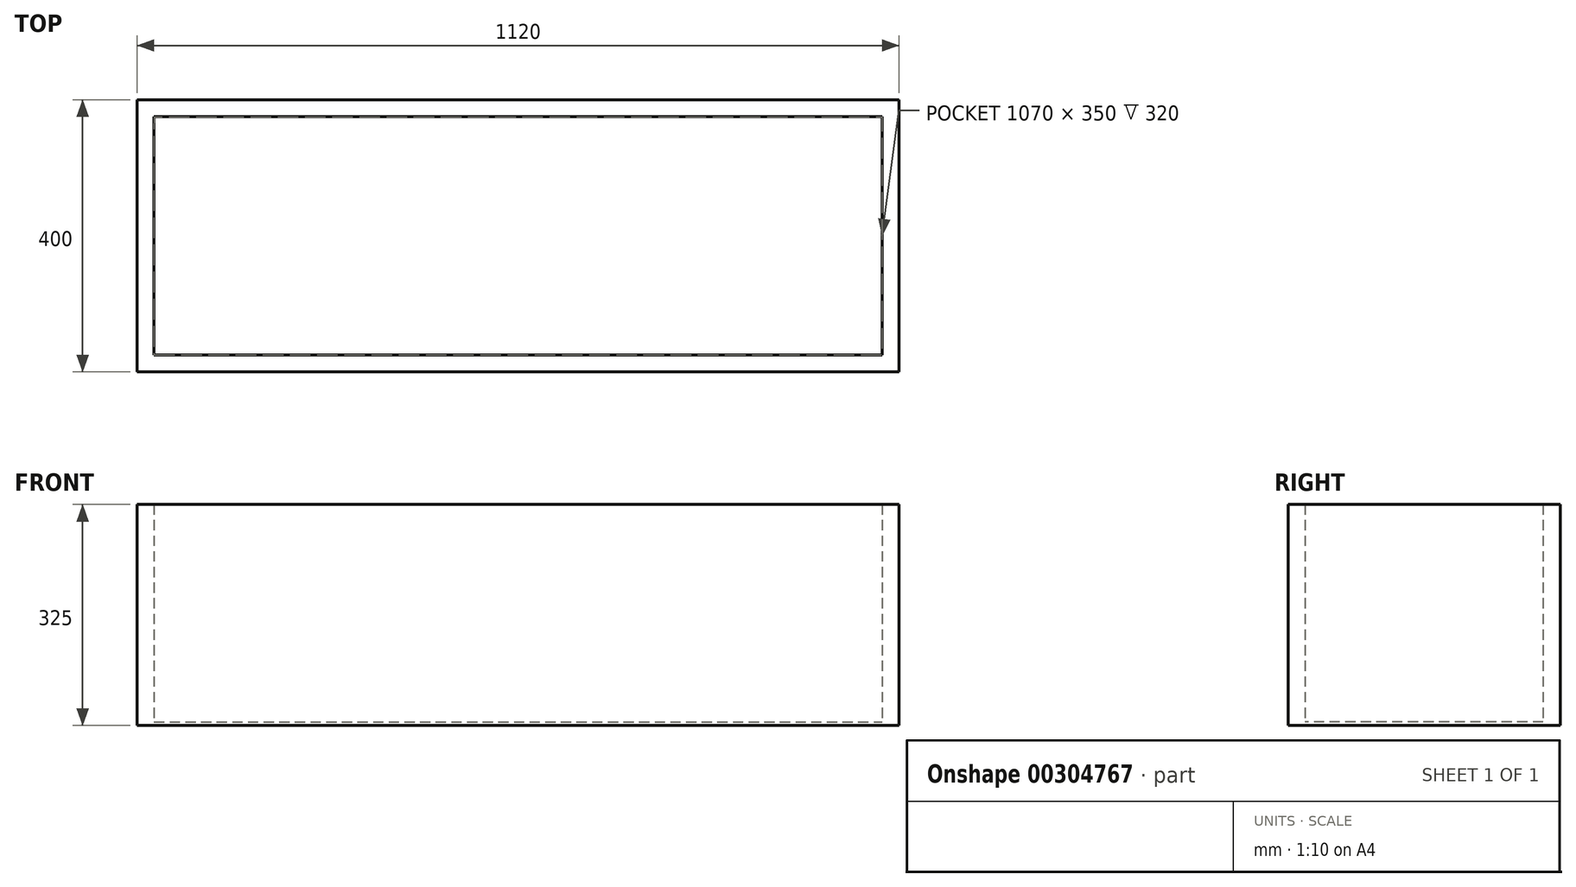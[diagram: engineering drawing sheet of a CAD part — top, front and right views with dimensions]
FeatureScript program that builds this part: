
annotation { "Feature Type Name" : "Feature", "Feature Type Description" : "" }
export const myFeature = defineFeature(function(context is Context, id is Id, definition is map)
    precondition{}
    {
        {
            var Q0;
            Q0=qCreatedBy(makeId("Top.planeOp"),FACE);
            var sketch = newSketch(context, id + "F0", { "sketchPlane" : qUnion([Q0])});
            skLineSegment(sketch, "E0.bottom", {"start": v(-560, 200) * mm, "end": v(560, 200) * mm});
            skLineSegment(sketch, "E0.top", {"start": v(-560, -200) * mm, "end": v(560, -200) * mm});
            skLineSegment(sketch, "E0.left", {"start": v(-560, 200) * mm, "end": v(-560, -200) * mm});
            skLineSegment(sketch, "E0.right", {"start": v(560, 200) * mm, "end": v(560, -200) * mm});
            skPoint(sketch, "E0.middle", {"position": v(0, 0) * mm});
            skLineSegment(sketch, "E1.0", {"start": v(-535, 175) * mm, "end": v(-535, -175) * mm});
            skLineSegment(sketch, "E1.1", {"start": v(-535, 175) * mm, "end": v(535, 175) * mm});
            skLineSegment(sketch, "E1.2", {"start": v(535, 175) * mm, "end": v(535, -175) * mm});
            skLineSegment(sketch, "E1.3", {"start": v(-535, -175) * mm, "end": v(535, -175) * mm});
            skSolve(sketch);
        }
        {
            var Q0;
            Q0=makeQuery(id+"F0.imprint","IMPRINT",FACE,{"disambiguationData":[TD([[makeQuery(id+"F0.imprint","IMPRINT",EDGE,{"derivedFrom":sQuery(id+"F0.wireOp",EDGE,"E0.bottom")}),-1.0]])]});
            extrude(context, id + "F1", {"entities" : qUnion([Q0]), "offsetDistance" : 25 * mm, "depth" : 320 * mm});
        }
        {
            var Q0;
            Q0=makeQuery(id+"F1.opExtrude","CAP_FACE",FACE,{"disambiguationData":[OSD([sQuery(id+"F0.wireOp",EDGE,"E0.bottom"),sQuery(id+"F0.wireOp",EDGE,"E0.top"),sQuery(id+"F0.wireOp",EDGE,"E0.left"),sQuery(id+"F0.wireOp",EDGE,"E0.right"),sQuery(id+"F0.wireOp",EDGE,"E1.0"),sQuery(id+"F0.wireOp",EDGE,"E1.1"),sQuery(id+"F0.wireOp",EDGE,"E1.2"),sQuery(id+"F0.wireOp",EDGE,"E1.3")])],"isStart":true});
            var sketch = newSketch(context, id + "F2", { "sketchPlane" : qUnion([Q0])});
            skLineSegment(sketch, "E2.0", {"start": v(-560, -200) * mm, "end": v(-560, 200) * mm});
            skLineSegment(sketch, "E3.0", {"start": v(-560, 200) * mm, "end": v(560, 200) * mm});
            skLineSegment(sketch, "E4.0", {"start": v(560, -200) * mm, "end": v(560, 200) * mm});
            skLineSegment(sketch, "E5.0", {"start": v(-560, -200) * mm, "end": v(560, -200) * mm});
            skSolve(sketch);
        }
        {
            var Q0;
            Q0=makeQuery(id+"F2.imprint","IMPRINT",FACE,{"disambiguationData":[TD([[makeQuery(id+"F2.imprint","IMPRINT",EDGE,{"derivedFrom":makeQuery(id+"F1.opExtrude","CAP_EDGE",EDGE,{"disambiguationData":[OSD([sQuery(id+"F0.wireOp",EDGE,"E1.0")])],"isStart":true})}),-1.0]])]});
            var Q1;
            Q1=makeQuery(id+"F2.imprint","IMPRINT",FACE,{"disambiguationData":[TD([[makeQuery(id+"F2.imprint","IMPRINT",EDGE,{"derivedFrom":sQuery(id+"F2.wireOp",EDGE,"E2.0")}),-1.0]])]});
            extrude(context, id + "F3", {"entities" : qUnion([Q0, Q1]), "operationType" : NewBodyOperationType.ADD, "depth" : 5 * mm});
        }
    });
